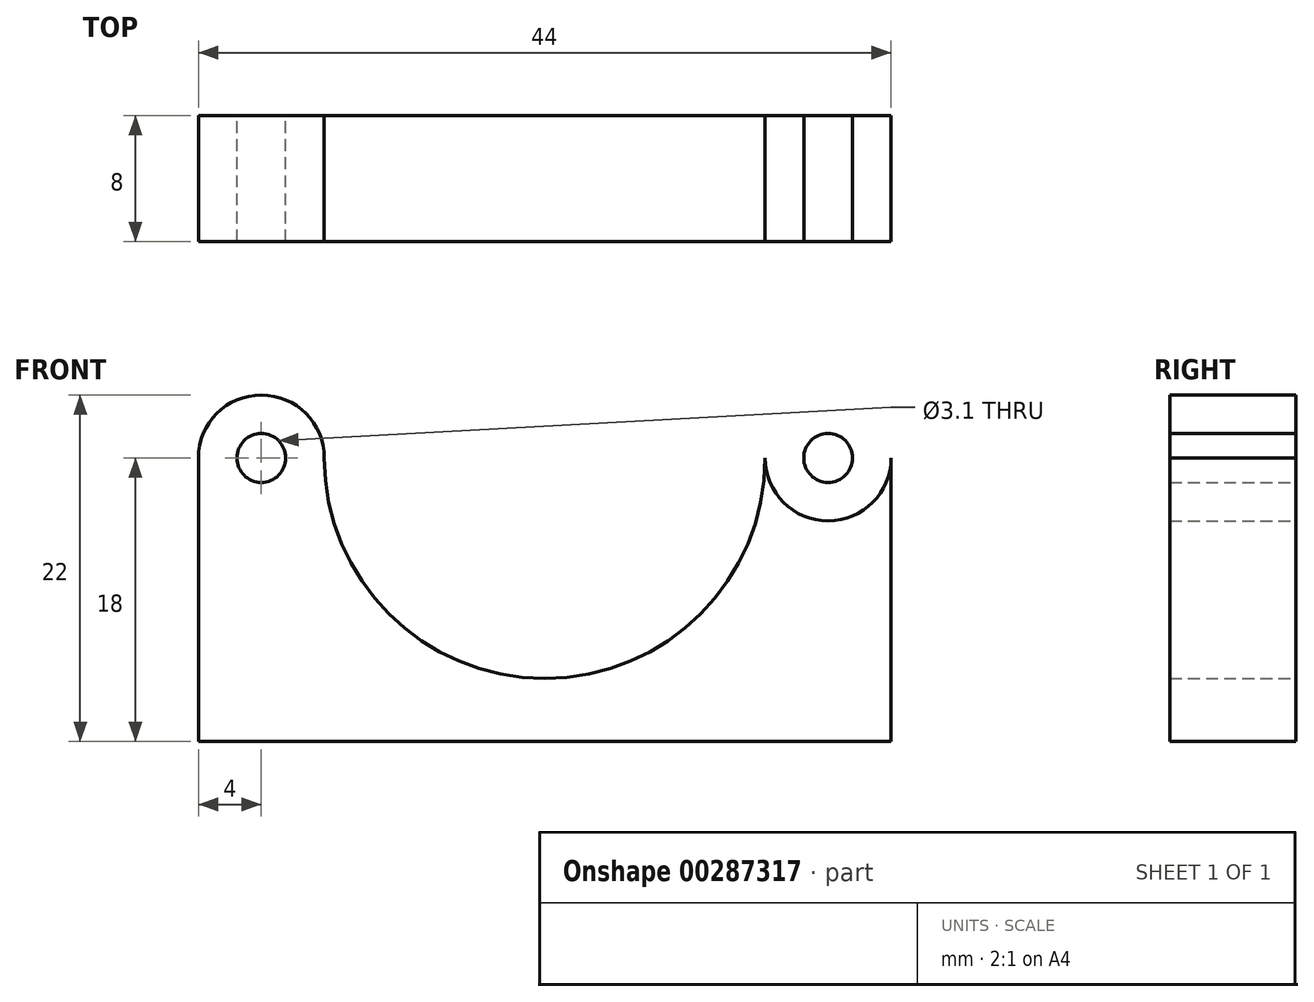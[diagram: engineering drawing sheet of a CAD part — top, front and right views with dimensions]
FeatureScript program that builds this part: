
annotation { "Feature Type Name" : "Feature", "Feature Type Description" : "" }
export const myFeature = defineFeature(function(context is Context, id is Id, definition is map)
    precondition{}
    {
        {
            var Q0;
            Q0=qCreatedBy(makeId("Front.planeOp"),FACE);
            var sketch = newSketch(context, id + "F0", { "sketchPlane" : qUnion([Q0])});
            skCircle(sketch, "E0", {"center": v(-18, 0) * mm, "radius": 1.55 * mm});
            skCircle(sketch, "E1.MirrorC", {"center": v(18, 0) * mm, "radius": 1.55 * mm});
            skCircle(sketch, "E2", {"center": v(-18, 0) * mm, "radius": 4 * mm});
            skCircle(sketch, "E3.MirrorC", {"center": v(18, 0) * mm, "radius": 4 * mm});
            skLineSegment(sketch, "E4", {"start": v(-22, 0) * mm, "end": v(-22, -18) * mm});
            skLineSegment(sketch, "E5", {"start": v(-22, -18) * mm, "end": v(22, -18) * mm});
            skLineSegment(sketch, "E6", {"start": v(22, -18) * mm, "end": v(22, 0) * mm});
            skArc(sketch, "E7", {"start": v(-14, 0) * mm, "mid": v(0, -14) * mm, "end": v(14, 0) * mm});
            skSolve(sketch);
        }
        {
            var Q0;
            {var subQ0=sQuery(id+"F0.wireOp",EDGE,"E4");Q0=makeQuery(id+"F0.imprint","IMPRINT",FACE,{"disambiguationData":[TD([[makeQuery(id+"F0.imprint","IMPRINT",EDGE,{"derivedFrom":subQ0}),1.0]])]});}
            var Q1;
            Q1=makeQuery(id+"F0.imprint","IMPRINT",FACE,{"disambiguationData":[TD([[makeQuery(id+"F0.imprint","IMPRINT",EDGE,{"derivedFrom":sQuery(id+"F0.wireOp",EDGE,"E0")}),-1.0]])]});
            var Q2;
            Q2=makeQuery(id+"F0.imprint","IMPRINT",FACE,{"disambiguationData":[TD([[makeQuery(id+"F0.imprint","IMPRINT",EDGE,{"derivedFrom":sQuery(id+"F0.wireOp",EDGE,"E1.MirrorC")}),1.0]])]});
            extrude(context, id + "F1", {"entities" : qUnion([Q0, Q1, Q2]), "depth" : 8 * mm});
        }
    });
